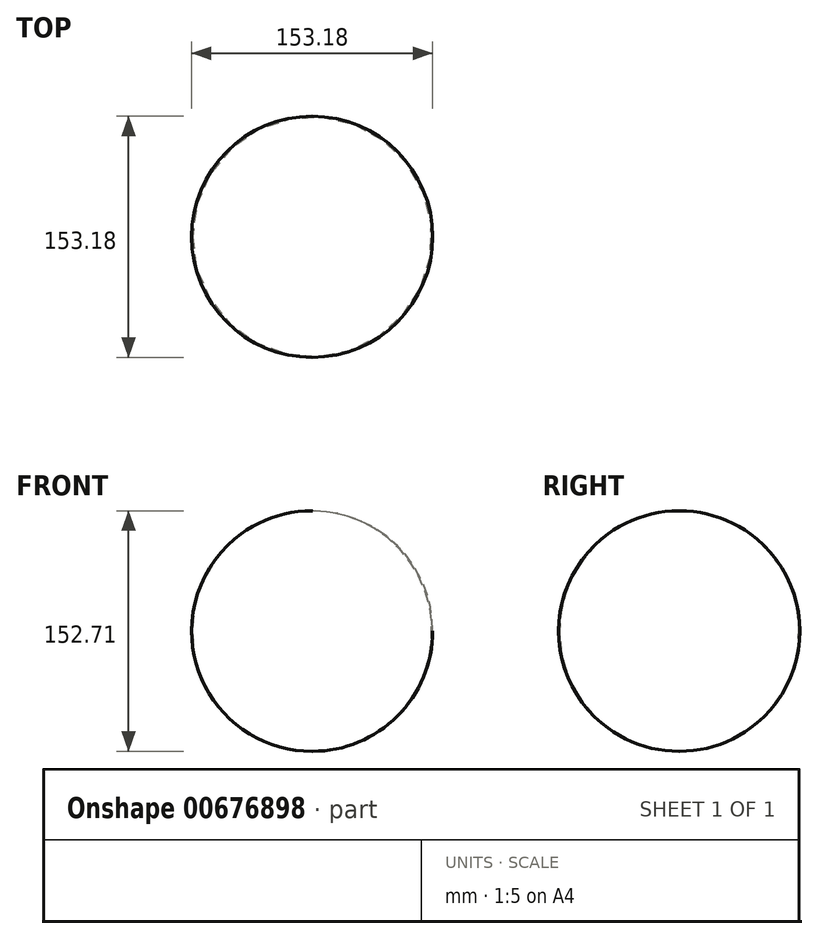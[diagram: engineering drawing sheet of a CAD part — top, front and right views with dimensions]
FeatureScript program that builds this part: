
annotation { "Feature Type Name" : "Feature", "Feature Type Description" : "" }
export const myFeature = defineFeature(function(context is Context, id is Id, definition is map)
    precondition{}
    {
        {
            var Q0;
            Q0=qCreatedBy(makeId("Front.planeOp"),FACE);
            var sketch = newSketch(context, id + "F0", { "sketchPlane" : qUnion([Q0])});
            skLineSegment(sketch, "E0", {"start": v(0, 75.7) * mm, "end": v(0, -77) * mm});
            skArc(sketch, "E1", {"start": v(0, -77) * mm, "mid": v(76.12, -0.65) * mm, "end": v(0, 75.7) * mm});
            skSolve(sketch);
        }
        {
            var Q0;
            Q0=makeQuery(id+"F0.imprint","IMPRINT",FACE,{"disambiguationData":[TD([[makeQuery(id+"F0.imprint","IMPRINT",EDGE,{"derivedFrom":sQuery(id+"F0.wireOp",EDGE,"E0")}),1.0]])]});
            var Q1;
            Q1=sQuery(id+"F0.wireOp",EDGE,"E0");
            revolve(context, id + "F1", {"entities" : qUnion([Q0]), "axis" : qUnion([Q1]), "revolveType" : RevolveType.FULL});
        }
        {
            var Q0;
            Q0=qCreatedBy(makeId("Top.planeOp"),FACE);
            cPlane(context, id + "F2", {"entities" : qUnion([Q0]), "cplaneType" : CPlaneType.OFFSET, "offset" : 25.4 * mm, "width" : 152.4 * mm, "height" : 152.4 * mm});
        }
    });
